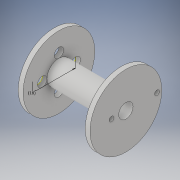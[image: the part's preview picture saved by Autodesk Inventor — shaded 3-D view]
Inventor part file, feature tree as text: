
AUTODESK INVENTOR PART (.ipt)
format: ipt  version: 2019 (Build 230136000, 136)  size: 152,576 bytes
history: native  units: in
note: dims shown in document units (in); Inventor stores cm internally (conversion verified against a paired STEP export)
features: sketch x6, extrude x2, revolve x1
ambient origin geometry x8: Origin, YZ Plane, XZ Plane, XY Plane, X Axis, Y Axis, Z Axis, Center Point
bodies: Solid1 (feature_tree)
feature tree (9):
  revolve  "Revolution1"  [1 undecoded]
  sketch  "Sketch2"  dims[d2=1.0236in d3=0.0787in]
  sketch  "Sketch3"  dims[d4=0.4724in d5=0.1181in]
  extrude  "Extrusion1"  Depth=0.0787in
  extrude  "Extrusion2"  Depth=0.1181in
  sketch  "Sketch5"  dims[d7=90.0deg]
  sketch  "Sketch6"  dims[d8=0.1575in d10=0.1575in d13=0.1575in d14=0.1575in d17=0.2756in d18=0.2756in d19=0.2756in d20=0.2756in d21=0.0787in d22=0.0in d23=0.0787in d24=0.0787in d25=0.2362in d26=0.5118in d27=0.0787in d28=0.0in d29=0.7087in]
  sketch  "Sketch1"  dims[d0=0.0787in d1=0.3937in]
  sketch  "Sketch4"  dims[d6=1.1811in]
note: 1 required parameter value undecoded (feature->parameter linkage not recoverable at this tier; creation-order binding heuristic only, values carry confidence <= 0.55)
